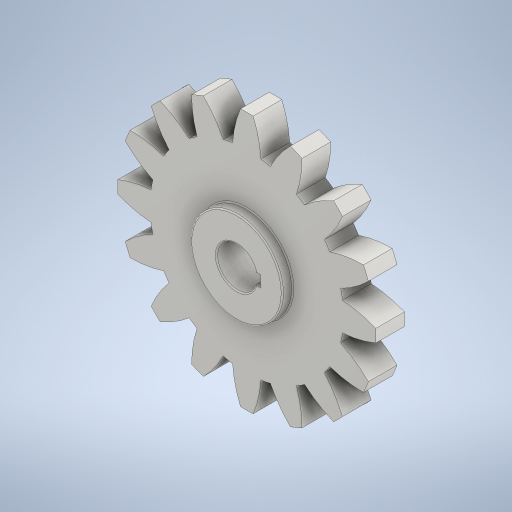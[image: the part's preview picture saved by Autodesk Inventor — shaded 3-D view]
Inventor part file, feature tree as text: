
AUTODESK INVENTOR PART (.ipt)
format: ipt  version: 2024.2 (Build 282272000, 272)  size: 573,952 bytes
history: native  units: mm (DEFAULTED — no unit token found)
features: other x5, extrude x4, sketch x4, plane x3, fillet x1, projected_geometry x1
ambient origin geometry x8: Origin, YZ Plane, XZ Plane, XY Plane, X Axis, Y Axis, Z Axis, Center Point
bodies: Solid1 (feature_tree)
feature tree (18):
  extrude  "Extrusion1"  Depth=25.0mm TaperAngle=0.0deg
  plane  "Work Plane2"
  plane  "Work Plane8"
  plane  "Work Plane9"
  other  "Spur Gear"
  extrude  "Extrusion2"  Depth=10.0mm TaperAngle=0.0deg
  extrude  "Extrusion3"  Depth=1.963495mm TaperAngle=0.0deg
  extrude  "Extrusion4"  TaperAngle=0.0deg  [1 undecoded]
  fillet  "Fillet1"  Radius=494.0mm
  other  "A-Side Definition"
  sketch  "Sketch1"  dims[d0=225.11376mm d1=25.0mm d2=0.0mm]
  other  "Srf1"
  sketch  "Sketch3"  dims[d3=200.10112mm d4=10.0mm d5=0.0mm]
  projected_geometry  "Projected Loop1"
  sketch  "Sketch5"  dims[d16=494.0mm d17=0.0mm d34=1.963495mm]
  sketch  "Sketch6"  dims[d39=0.0mm d41=0.0mm d43=494.0mm d46=494.0mm d47=0.0mm d48=0.0mm d51=35.0mm d52=0.0mm d53=0.0mm d55=80.0mm d56=35.0mm d57=9.0mm d58=0.0mm d59=21.0mm d60=10.0mm d61=0.0mm d62=0.0mm d63=1.0mm]
  other  "Pitch Diameter"
  other  "Definition1"
note: 1 required parameter value undecoded (feature->parameter linkage not recoverable at this tier; creation-order binding heuristic only, values carry confidence <= 0.55)
